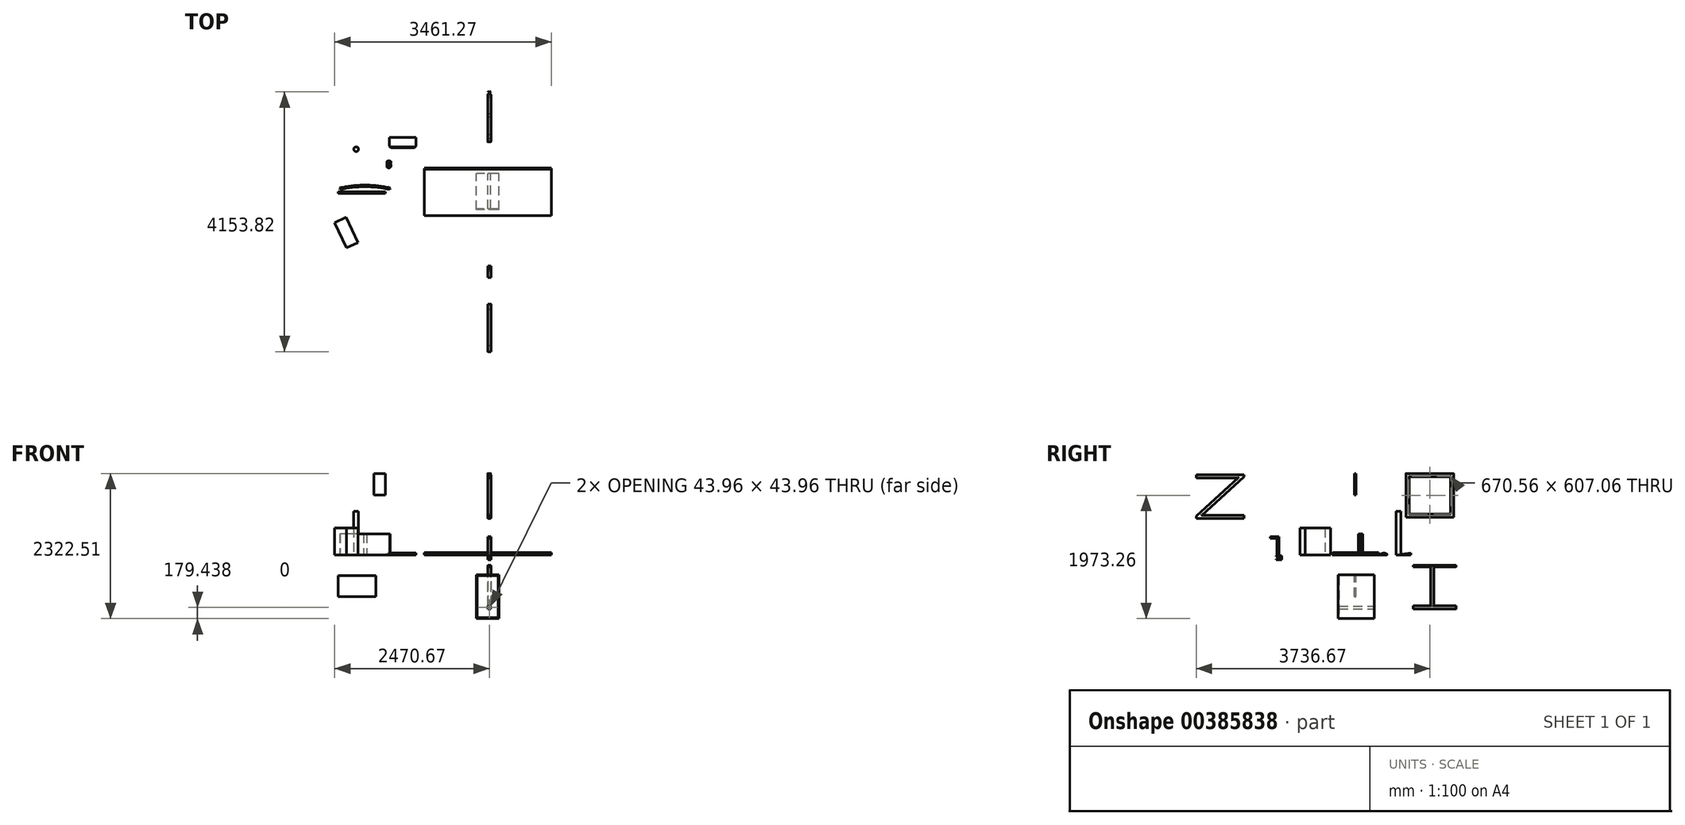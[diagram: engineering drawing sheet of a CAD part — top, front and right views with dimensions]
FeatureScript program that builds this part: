
annotation { "Feature Type Name" : "Feature", "Feature Type Description" : "" }
export const myFeature = defineFeature(function(context is Context, id is Id, definition is map)
    precondition{}
    {
        {
            var Q0;
            Q0=qCreatedBy(makeId("Top.planeOp"),FACE);
            var sketch = newSketch(context, id + "F0", { "sketchPlane" : qUnion([Q0])});
            skLineSegment(sketch, "E0.bottom", {"start": v(1016, -381) * mm, "end": v(-1016, -381) * mm});
            skLineSegment(sketch, "E0.top", {"start": v(1016, 381) * mm, "end": v(-1016, 381) * mm});
            skLineSegment(sketch, "E0.left", {"start": v(1016, -381) * mm, "end": v(1016, 381) * mm});
            skLineSegment(sketch, "E0.right", {"start": v(-1016, -381) * mm, "end": v(-1016, 381) * mm});
            skPoint(sketch, "E0.middle", {"position": v(0, 0) * mm});
            skSolve(sketch);
        }
        {
            var Q0;
            Q0=makeQuery(id+"F0.imprint","IMPRINT",FACE,{"disambiguationData":[TD([[makeQuery(id+"F0.imprint","IMPRINT",EDGE,{"derivedFrom":sQuery(id+"F0.wireOp",EDGE,"E0.bottom")}),-1.0]])]});
            extrude(context, id + "F1", {"entities" : qUnion([Q0]), "depth" : 38.1 * mm});
        }
        {
            var Q0;
            Q0=makeQuery(id+"F1.opExtrude","CAP_EDGE",EDGE,{"disambiguationData":[OSD([sQuery(id+"F0.wireOp",EDGE,"E0.bottom")])],"isStart":false});
            fillet(context, id + "F2", {"entities" : qUnion([Q0]), "radius" : 12.7 * mm, "tangentPropagation" : true, "allowEdgeOverflow" : false});
        }
        {
            var Q0;
            Q0=qCreatedBy(makeId("Top.planeOp"),FACE);
            cPlane(context, id + "F3", {"entities" : qUnion([Q0]), "cplaneType" : CPlaneType.OFFSET, "offset" : 1016 * mm, "oppositeDirection" : true, "width" : 152.4 * mm, "height" : 152.4 * mm});
        }
        {
            var Q0;
            Q0=qCreatedBy(id+"F3.planeOp",FACE);
            var sketch = newSketch(context, id + "F4", { "sketchPlane" : qUnion([Q0])});
            skLineSegment(sketch, "E1.bottom", {"start": v(179.32, -290.83) * mm, "end": v(-179.32, -290.83) * mm});
            skLineSegment(sketch, "E1.top", {"start": v(179.32, 290.83) * mm, "end": v(-179.32, 290.83) * mm});
            skLineSegment(sketch, "E1.left", {"start": v(179.32, -290.83) * mm, "end": v(179.32, 290.83) * mm});
            skLineSegment(sketch, "E1.right", {"start": v(-179.32, -290.83) * mm, "end": v(-179.32, 290.83) * mm});
            skPoint(sketch, "E1.middle", {"position": v(0, 0) * mm});
            skSolve(sketch);
        }
        {
            var Q0;
            Q0 = qSketchRegion(id + "F4", true);
            extrude(context, id + "F5", {"entities" : qUnion([Q0]), "depth" : 698.5 * mm});
        }
        {
            var Q0;
            Q0=makeQuery(id+"F5.opExtrude","SWEPT_FACE",FACE,{"disambiguationData":[OSD([sQuery(id+"F4.wireOp",EDGE,"E1.bottom")])]});
            var sketch = newSketch(context, id + "F6", { "sketchPlane" : qUnion([Q0])});
            skLineSegment(sketch, "E2.0", {"start": v(166.62, -330.2) * mm, "end": v(166.62, -1003.3) * mm});
            skLineSegment(sketch, "E2.1", {"start": v(166.62, -330.2) * mm, "end": v(-166.62, -330.2) * mm});
            skLineSegment(sketch, "E2.2", {"start": v(-166.62, -330.2) * mm, "end": v(-166.62, -1003.3) * mm});
            skLineSegment(sketch, "E2.3", {"start": v(166.62, -1003.3) * mm, "end": v(-166.62, -1003.3) * mm});
            skSolve(sketch);
        }
        {
            var Q0;
            Q0 = qSketchRegion(id + "F6", true);
            extrude(context, id + "F7", {"entities" : qUnion([Q0]), "operationType" : NewBodyOperationType.REMOVE, "oppositeDirection" : true, "depth" : 12.7 * mm});
        }
        {
            var Q0;
            Q0=qCreatedBy(makeId("Right.planeOp"),FACE);
            var sketch = newSketch(context, id + "F8", { "sketchPlane" : qUnion([Q0])});
            skLineSegment(sketch, "E3", {"start": v(1595.15, -163.46) * mm, "end": v(1595.15, -188.86) * mm});
            skLineSegment(sketch, "E4", {"start": v(1595.15, -188.86) * mm, "end": v(1239.55, -188.86) * mm});
            skLineSegment(sketch, "E5", {"start": v(1239.55, -188.86) * mm, "end": v(1239.55, -811.16) * mm});
            skLineSegment(sketch, "E6", {"start": v(1239.55, -811.16) * mm, "end": v(1595.15, -811.16) * mm});
            skLineSegment(sketch, "E7", {"start": v(1595.15, -811.16) * mm, "end": v(1595.15, -861.96) * mm});
            skLineSegment(sketch, "E8", {"start": v(1595.15, -861.96) * mm, "end": v(909.35, -861.96) * mm});
            skLineSegment(sketch, "E9", {"start": v(909.35, -861.96) * mm, "end": v(909.35, -811.16) * mm});
            skLineSegment(sketch, "E10", {"start": v(909.35, -811.16) * mm, "end": v(1188.75, -811.16) * mm});
            skLineSegment(sketch, "E11", {"start": v(1188.75, -811.16) * mm, "end": v(1188.75, -188.86) * mm});
            skLineSegment(sketch, "E12", {"start": v(1188.75, -188.86) * mm, "end": v(909.35, -188.86) * mm});
            skLineSegment(sketch, "E13", {"start": v(909.35, -188.86) * mm, "end": v(909.35, -163.46) * mm});
            skLineSegment(sketch, "E14", {"start": v(1595.15, -163.46) * mm, "end": v(909.35, -163.46) * mm});
            skSolve(sketch);
        }
        {
            var Q0;
            Q0=makeQuery(id+"F8.imprint","IMPRINT",FACE,{"disambiguationData":[TD([[makeQuery(id+"F8.imprint","IMPRINT",EDGE,{"derivedFrom":sQuery(id+"F8.wireOp",EDGE,"E3")}),-1.0]])]});
            extrude(context, id + "F9", {"entities" : qUnion([Q0]), "depth" : 50.8 * mm});
        }
        {
            var Q0;
            Q0=makeQuery(id+"F9.opExtrude","CAP_EDGE",EDGE,{"disambiguationData":[OSD([sQuery(id+"F8.wireOp",EDGE,"E6")])],"isStart":false});
            var Q1;
            Q1=makeQuery(id+"F9.opExtrude","CAP_EDGE",EDGE,{"disambiguationData":[OSD([sQuery(id+"F8.wireOp",EDGE,"E8")])],"isStart":false});
            var Q2;
            Q2=makeQuery(id+"F9.opExtrude","CAP_EDGE",EDGE,{"disambiguationData":[OSD([sQuery(id+"F8.wireOp",EDGE,"E10")])],"isStart":false});
            var Q3;
            Q3=makeQuery(id+"F9.opExtrude","CAP_EDGE",EDGE,{"disambiguationData":[OSD([sQuery(id+"F8.wireOp",EDGE,"E11")])],"isStart":false});
            var Q4;
            Q4=makeQuery(id+"F9.opExtrude","CAP_EDGE",EDGE,{"disambiguationData":[OSD([sQuery(id+"F8.wireOp",EDGE,"E5")])],"isStart":false});
            var Q5;
            Q5=makeQuery(id+"F9.opExtrude","CAP_EDGE",EDGE,{"disambiguationData":[OSD([sQuery(id+"F8.wireOp",EDGE,"E5")])],"isStart":true});
            var Q6;
            Q6=makeQuery(id+"F9.opExtrude","CAP_EDGE",EDGE,{"disambiguationData":[OSD([sQuery(id+"F8.wireOp",EDGE,"E6")])],"isStart":true});
            var Q7;
            Q7=makeQuery(id+"F9.opExtrude","CAP_EDGE",EDGE,{"disambiguationData":[OSD([sQuery(id+"F8.wireOp",EDGE,"E10")])],"isStart":true});
            var Q8;
            Q8=makeQuery(id+"F9.opExtrude","CAP_EDGE",EDGE,{"disambiguationData":[OSD([sQuery(id+"F8.wireOp",EDGE,"E8")])],"isStart":true});
            var Q9;
            Q9=makeQuery(id+"F9.opExtrude","CAP_EDGE",EDGE,{"disambiguationData":[OSD([sQuery(id+"F8.wireOp",EDGE,"E11")])],"isStart":true});
            var Q10;
            Q10=makeQuery(id+"F9.opExtrude","CAP_EDGE",EDGE,{"disambiguationData":[OSD([sQuery(id+"F8.wireOp",EDGE,"E14")])],"isStart":true});
            var Q11;
            Q11=makeQuery(id+"F9.opExtrude","CAP_EDGE",EDGE,{"disambiguationData":[OSD([sQuery(id+"F8.wireOp",EDGE,"E12")])],"isStart":true});
            var Q12;
            Q12=makeQuery(id+"F9.opExtrude","CAP_EDGE",EDGE,{"disambiguationData":[OSD([sQuery(id+"F8.wireOp",EDGE,"E4")])],"isStart":true});
            var Q13;
            Q13=makeQuery(id+"F9.opExtrude","CAP_EDGE",EDGE,{"disambiguationData":[OSD([sQuery(id+"F8.wireOp",EDGE,"E14")])],"isStart":false});
            var Q14;
            Q14=makeQuery(id+"F9.opExtrude","CAP_EDGE",EDGE,{"disambiguationData":[OSD([sQuery(id+"F8.wireOp",EDGE,"E4")])],"isStart":false});
            var Q15;
            Q15=makeQuery(id+"F9.opExtrude","CAP_EDGE",EDGE,{"disambiguationData":[OSD([sQuery(id+"F8.wireOp",EDGE,"E12")])],"isStart":false});
            fillet(context, id + "F10", {"entities" : qUnion([Q0, Q1, Q2, Q3, Q4, Q5, Q6, Q7, Q8, Q9, Q10, Q11, Q12, Q13, Q14, Q15]), "radius" : 5.08 * mm, "tangentPropagation" : true, "allowEdgeOverflow" : false});
        }
        {
            var Q0;
            Q0=makeQuery(id+"F9.opExtrude","SWEPT_FACE",FACE,{"disambiguationData":[OSD([sQuery(id+"F8.wireOp",EDGE,"E7")])]});
            var sketch = newSketch(context, id + "F11", { "sketchPlane" : qUnion([Q0])});
            skLineSegment(sketch, "E15.bottom", {"start": v(-5.96, -858.54) * mm, "end": v(-44.84, -858.54) * mm});
            skLineSegment(sketch, "E15.top", {"start": v(-5.96, -814.58) * mm, "end": v(-44.84, -814.58) * mm});
            skLineSegment(sketch, "E15.left", {"start": v(-3.42, -856) * mm, "end": v(-3.42, -817.12) * mm});
            skLineSegment(sketch, "E15.right", {"start": v(-47.38, -856) * mm, "end": v(-47.38, -817.12) * mm});
            skPoint(sketch, "E15.middle", {"position": v(-25.4, -836.56) * mm});
            skPoint(sketch, "E16.trimOffspring.end.orphan", {"position": v(-1.49, -860.47) * mm});
            skPoint(sketch, "E17.start.orphan", {"position": v(-49.31, -812.65) * mm});
            skPoint(sketch, "E18.visualSharp", {"position": v(-47.38, -814.58) * mm});
            skArc(sketch, "E18.filletArc", {"start": v(-44.84, -814.58) * mm, "mid": v(-46.64, -815.32) * mm, "end": v(-47.38, -817.12) * mm});
            skPoint(sketch, "E19.visualSharp", {"position": v(-47.38, -858.54) * mm});
            skArc(sketch, "E19.filletArc", {"start": v(-47.38, -856) * mm, "mid": v(-46.64, -857.8) * mm, "end": v(-44.84, -858.54) * mm});
            skPoint(sketch, "E20.visualSharp", {"position": v(-3.42, -858.54) * mm});
            skArc(sketch, "E20.filletArc", {"start": v(-5.96, -858.54) * mm, "mid": v(-4.16, -857.8) * mm, "end": v(-3.42, -856) * mm});
            skPoint(sketch, "E21.visualSharp", {"position": v(-3.42, -814.58) * mm});
            skArc(sketch, "E21.filletArc", {"start": v(-3.42, -817.12) * mm, "mid": v(-4.16, -815.32) * mm, "end": v(-5.96, -814.58) * mm});
            skSolve(sketch);
        }
        {
            var Q0;
            Q0 = qSketchRegion(id + "F11", true);
            extrude(context, id + "F12", {"entities" : qUnion([Q0]), "operationType" : NewBodyOperationType.REMOVE, "endBound" : BoundingType.THROUGH_ALL, "oppositeDirection" : true, "depth" : 25.4 * mm});
        }
        {
            var Q0;
            Q0=qCreatedBy(makeId("Top.planeOp"),FACE);
            var sketch = newSketch(context, id + "F13", { "sketchPlane" : qUnion([Q0])});
            skLineSegment(sketch, "E22", {"start": v(-2361.1, 34.13) * mm, "end": v(-1563.54, 34.13) * mm, "construction": true});
            skArc(sketch, "E23", {"start": v(-1563.54, 34.13) * mm, "mid": v(-1962.32, 78.9) * mm, "end": v(-2361.1, 34.13) * mm});
            skArc(sketch, "E24.0.1.0", {"start": v(-1563.54, 59.53) * mm, "mid": v(-1962.32, 104.3) * mm, "end": v(-2361.1, 59.53) * mm});
            skLineSegment(sketch, "E24.direction1", {"start": v(-1962.32, -1719.42) * mm, "end": v(-1848.02, -1719.42) * mm, "construction": true});
            skLineSegment(sketch, "E24.direction2", {"start": v(-1962.32, -1719.42) * mm, "end": v(-1962.32, -1694.02) * mm, "construction": true});
            skLineSegment(sketch, "E25", {"start": v(-2361.1, 34.13) * mm, "end": v(-2373.8, 34.13) * mm});
            skLineSegment(sketch, "E26", {"start": v(-2373.8, 34.13) * mm, "end": v(-2361.1, 59.53) * mm});
            skLineSegment(sketch, "E27", {"start": v(-1563.54, 34.13) * mm, "end": v(-1550.84, 34.13) * mm});
            skLineSegment(sketch, "E28", {"start": v(-1550.84, 34.13) * mm, "end": v(-1563.54, 59.53) * mm});
            skSolve(sketch);
        }
        {
            var Q0;
            Q0 = qSketchRegion(id + "F13", true);
            extrude(context, id + "F14", {"entities" : qUnion([Q0]), "depth" : 340.36 * mm});
        }
        {
            var Q0;
            Q0=qCreatedBy(makeId("Front.planeOp"),FACE);
            var sketch = newSketch(context, id + "F15", { "sketchPlane" : qUnion([Q0])});
            skLineSegment(sketch, "E29.bottom", {"start": v(-1789.8, -664.85) * mm, "end": v(-2389.23, -664.85) * mm});
            skLineSegment(sketch, "E29.top", {"start": v(-1789.8, -324.49) * mm, "end": v(-2389.23, -324.49) * mm});
            skLineSegment(sketch, "E29.left", {"start": v(-1789.8, -664.85) * mm, "end": v(-1789.8, -324.49) * mm});
            skLineSegment(sketch, "E29.right", {"start": v(-2389.23, -664.85) * mm, "end": v(-2389.23, -324.49) * mm});
            skPoint(sketch, "E29.middle", {"position": v(-2089.51, -494.67) * mm});
            skSolve(sketch);
        }
        {
            var Q0;
            Q0 = qSketchRegion(id + "F15", true);
            extrude(context, id + "F16", {"entities" : qUnion([Q0]), "depth" : 25.4 * mm});
        }
        {
            var Q0;
            Q0=qCreatedBy(makeId("Right.planeOp"),FACE);
            var sketch = newSketch(context, id + "F17", { "sketchPlane" : qUnion([Q0])});
            skLineSegment(sketch, "E30", {"start": v(-1280.87, -22.9) * mm, "end": v(-1204.67, -22.9) * mm});
            skLineSegment(sketch, "E31", {"start": v(-1204.67, -22.9) * mm, "end": v(-1204.67, -61) * mm});
            skLineSegment(sketch, "E32", {"start": v(-1204.67, -61) * mm, "end": v(-1280.87, -61) * mm});
            skLineSegment(sketch, "E33", {"start": v(-1280.87, -61) * mm, "end": v(-1280.87, -73.7) * mm});
            skLineSegment(sketch, "E34", {"start": v(-1280.87, -73.7) * mm, "end": v(-1191.97, -73.7) * mm});
            skLineSegment(sketch, "E35", {"start": v(-1191.97, -73.7) * mm, "end": v(-1191.97, -10.2) * mm});
            skLineSegment(sketch, "E36", {"start": v(-1191.97, -10.2) * mm, "end": v(-1235.72, -10.2) * mm});
            skLineSegment(sketch, "E37", {"start": v(-1235.72, -10.2) * mm, "end": v(-1235.72, 294.6) * mm});
            skLineSegment(sketch, "E38", {"start": v(-1235.72, 294.6) * mm, "end": v(-1372.65, 294.6) * mm});
            skLineSegment(sketch, "E39", {"start": v(-1372.65, 294.6) * mm, "end": v(-1372.65, 269.2) * mm});
            skLineSegment(sketch, "E40", {"start": v(-1372.65, 269.2) * mm, "end": v(-1268.74, 269.2) * mm});
            skLineSegment(sketch, "E41", {"start": v(-1268.74, 269.2) * mm, "end": v(-1268.74, -10.2) * mm});
            skLineSegment(sketch, "E42", {"start": v(-1280.87, -10.2) * mm, "end": v(-1280.87, -22.9) * mm});
            skLineSegment(sketch, "E43", {"start": v(-1268.74, -10.2) * mm, "end": v(-1280.87, -10.2) * mm});
            skSolve(sketch);
        }
        {
            var Q0;
            Q0 = qSketchRegion(id + "F17", true);
            extrude(context, id + "F18", {"entities" : qUnion([Q0]), "depth" : 50.8 * mm});
        }
        {
            var Q0;
            Q0=makeQuery(id+"F14.opExtrude","CAP_FACE",FACE,{"disambiguationData":[OSD([sQuery(id+"F13.wireOp",EDGE,"E23"),sQuery(id+"F13.wireOp",EDGE,"E24.0.1.0"),sQuery(id+"F13.wireOp",EDGE,"E25"),sQuery(id+"F13.wireOp",EDGE,"E26"),sQuery(id+"F13.wireOp",EDGE,"E27"),sQuery(id+"F13.wireOp",EDGE,"E28")])],"isStart":false});
            var sketch = newSketch(context, id + "F19", { "sketchPlane" : qUnion([Q0])});
            skLineSegment(sketch, "E44.bottom", {"start": v(-1936.92, 107.7) * mm, "end": v(-1987.72, 107.7) * mm});
            skLineSegment(sketch, "E44.top", {"start": v(-1936.92, 100.9) * mm, "end": v(-1987.72, 100.9) * mm});
            skLineSegment(sketch, "E44.left", {"start": v(-1936.92, 107.7) * mm, "end": v(-1936.92, 100.9) * mm});
            skLineSegment(sketch, "E44.right", {"start": v(-1987.72, 107.7) * mm, "end": v(-1987.72, 100.9) * mm});
            skPoint(sketch, "E44.middle", {"position": v(-1962.32, 104.3) * mm});
            skSolve(sketch);
        }
        {
            var Q0;
            Q0 = qSketchRegion(id + "F19", true);
            extrude(context, id + "F20", {"entities" : qUnion([Q0]), "operationType" : NewBodyOperationType.ADD, "oppositeDirection" : true, "depth" : 340.36 * mm});
        }
        {
            var Q0;
            Q0=makeQuery(id+"F20.boolean.opBoolean","MERGE",FACE,{"derivedFrom":[makeQuery(id+"F14.opExtrude","CAP_FACE",FACE,{"disambiguationData":[OSD([sQuery(id+"F13.wireOp",EDGE,"E23"),sQuery(id+"F13.wireOp",EDGE,"E24.0.1.0"),sQuery(id+"F13.wireOp",EDGE,"E25"),sQuery(id+"F13.wireOp",EDGE,"E26"),sQuery(id+"F13.wireOp",EDGE,"E27"),sQuery(id+"F13.wireOp",EDGE,"E28")])],"isStart":false}),makeQuery(id+"F20.opExtrude","CAP_FACE",FACE,{"disambiguationData":[OSD([sQuery(id+"F19.wireOp",EDGE,"E44.bottom"),sQuery(id+"F19.wireOp",EDGE,"E44.top"),sQuery(id+"F19.wireOp",EDGE,"E44.left"),sQuery(id+"F19.wireOp",EDGE,"E44.right")])],"isStart":true})]});
            var sketch = newSketch(context, id + "F21", { "sketchPlane" : qUnion([Q0])});
            skLineSegment(sketch, "E45", {"start": v(-2361.1, 34.13) * mm, "end": v(-2370.03, 75.5) * mm});
            skLineSegment(sketch, "E46", {"start": v(-2370.03, 75.5) * mm, "end": v(-2381.81, 26.86) * mm});
            skLineSegment(sketch, "E47", {"start": v(-2381.81, 26.86) * mm, "end": v(-2362.2, 27.05) * mm});
            skLineSegment(sketch, "E48", {"start": v(-2362.2, 27.05) * mm, "end": v(-2361.1, 34.13) * mm});
            skSolve(sketch);
        }
        {
            var Q0;
            Q0 = qSketchRegion(id + "F21", true);
            extrude(context, id + "F22", {"entities" : qUnion([Q0]), "operationType" : NewBodyOperationType.REMOVE, "oppositeDirection" : true, "depth" : 635 * mm});
        }
        {
            var Q0;
            Q0=qCreatedBy(makeId("Top.planeOp"),FACE);
            var sketch = newSketch(context, id + "F23", { "sketchPlane" : qUnion([Q0])});
            skLineSegment(sketch, "E49.bottom", {"start": v(-2076.25, -814.48) * mm, "end": v(-2276.14, -814.48) * mm});
            skLineSegment(sketch, "E49.top", {"start": v(-2076.25, -369.98) * mm, "end": v(-2276.14, -369.98) * mm});
            skLineSegment(sketch, "E49.left", {"start": v(-2076.25, -814.48) * mm, "end": v(-2076.25, -369.98) * mm});
            skLineSegment(sketch, "E49.right", {"start": v(-2276.14, -814.48) * mm, "end": v(-2276.14, -369.98) * mm});
            skPoint(sketch, "E49.middle", {"position": v(-2176.2, -592.23) * mm});
            skSolve(sketch);
        }
        {
            var Q0;
            Q0 = qSketchRegion(id + "F23", true);
            extrude(context, id + "F24", {"entities" : qUnion([Q0]), "depth" : 431.8 * mm});
        }
        {
            var Q0;
            Q0=makeQuery(id+"F24.opExtrude","SWEPT_BODY",BODY,{"disambiguationData":[OSD([sQuery(id+"F23.wireOp",EDGE,"E49.bottom"),sQuery(id+"F23.wireOp",EDGE,"E49.top"),sQuery(id+"F23.wireOp",EDGE,"E49.left"),sQuery(id+"F23.wireOp",EDGE,"E49.right")])]});
            var Q1;
            Q1=makeQuery(id+"F24.opExtrude","SWEPT_EDGE",EDGE,{"disambiguationData":[OSD([sQuery(id+"F23.wireOp",EDGE,"E49.bottom"),sQuery(id+"F23.wireOp",EDGE,"E49.left")])]});
            transform(context, id + "F25", {"entities" : qUnion([Q0]), "transformType" : TransformType.ROTATION, "transformAxis" : qUnion([Q1]), "angle" : 335 * degree, "makeCopy" : false});
        }
        {
            var Q0;
            Q0=qCreatedBy(makeId("Right.planeOp"),FACE);
            var sketch = newSketch(context, id + "F26", { "sketchPlane" : qUnion([Q0])});
            skLineSegment(sketch, "E50.bottom", {"start": v(1559, 608) * mm, "end": v(797, 608) * mm});
            skLineSegment(sketch, "E50.top", {"start": v(1559, 1306.5) * mm, "end": v(797, 1306.5) * mm});
            skLineSegment(sketch, "E50.left", {"start": v(1559, 608) * mm, "end": v(1559, 1306.5) * mm});
            skLineSegment(sketch, "E50.right", {"start": v(797, 608) * mm, "end": v(797, 1306.5) * mm});
            skPoint(sketch, "E50.middle", {"position": v(1178, 957.26) * mm});
            skLineSegment(sketch, "E51.0", {"start": v(1508.2, 1255.7) * mm, "end": v(847.8, 1255.7) * mm});
            skLineSegment(sketch, "E51.1", {"start": v(1508.2, 658.8) * mm, "end": v(1508.2, 1255.7) * mm});
            skLineSegment(sketch, "E51.2", {"start": v(1508.2, 658.8) * mm, "end": v(847.8, 658.8) * mm});
            skLineSegment(sketch, "E51.3", {"start": v(847.8, 658.8) * mm, "end": v(847.8, 1255.7) * mm});
            skSolve(sketch);
        }
        {
            var Q0;
            Q0=makeQuery(id+"F26.imprint","IMPRINT",FACE,{"disambiguationData":[TD([[makeQuery(id+"F26.imprint","IMPRINT",EDGE,{"derivedFrom":sQuery(id+"F26.wireOp",EDGE,"E50.bottom")}),-1.0]])]});
            extrude(context, id + "F27", {"entities" : qUnion([Q0]), "depth" : 50.8 * mm});
        }
        {
            var Q0;
            Q0=qCreatedBy(makeId("Top.planeOp"),FACE);
            var sketch = newSketch(context, id + "F28", { "sketchPlane" : qUnion([Q0])});
            skCircle(sketch, "E52", {"center": v(-2102.7, 679.67) * mm, "radius": 38.1 * mm});
            skSolve(sketch);
        }
        {
            var Q0;
            Q0 = qSketchRegion(id + "F28", true);
            extrude(context, id + "F29", {"entities" : qUnion([Q0]), "depth" : 698.5 * mm});
        }
        {
            var Q0;
            Q0=makeQuery(id+"F27.opExtrude","CAP_EDGE",EDGE,{"disambiguationData":[OSD([sQuery(id+"F26.wireOp",EDGE,"E50.right")])],"isStart":false});
            var Q1;
            Q1=makeQuery(id+"F27.opExtrude","CAP_EDGE",EDGE,{"disambiguationData":[OSD([sQuery(id+"F26.wireOp",EDGE,"E50.right")])],"isStart":true});
            var Q2;
            Q2=makeQuery(id+"F27.opExtrude","CAP_EDGE",EDGE,{"disambiguationData":[OSD([sQuery(id+"F26.wireOp",EDGE,"E51.3")])],"isStart":false});
            var Q3;
            Q3=makeQuery(id+"F27.opExtrude","CAP_EDGE",EDGE,{"disambiguationData":[OSD([sQuery(id+"F26.wireOp",EDGE,"E51.2")])],"isStart":false});
            var Q4;
            Q4=makeQuery(id+"F27.opExtrude","CAP_EDGE",EDGE,{"disambiguationData":[OSD([sQuery(id+"F26.wireOp",EDGE,"E50.bottom")])],"isStart":false});
            var Q5;
            Q5=makeQuery(id+"F27.opExtrude","CAP_EDGE",EDGE,{"disambiguationData":[OSD([sQuery(id+"F26.wireOp",EDGE,"E51.2")])],"isStart":true});
            var Q6;
            Q6=makeQuery(id+"F27.opExtrude","CAP_EDGE",EDGE,{"disambiguationData":[OSD([sQuery(id+"F26.wireOp",EDGE,"E50.bottom")])],"isStart":true});
            var Q7;
            Q7=makeQuery(id+"F27.opExtrude","CAP_EDGE",EDGE,{"disambiguationData":[OSD([sQuery(id+"F26.wireOp",EDGE,"E51.3")])],"isStart":true});
            var Q8;
            Q8=makeQuery(id+"F27.opExtrude","CAP_EDGE",EDGE,{"disambiguationData":[OSD([sQuery(id+"F26.wireOp",EDGE,"E51.1")])],"isStart":true});
            var Q9;
            Q9=makeQuery(id+"F27.opExtrude","CAP_EDGE",EDGE,{"disambiguationData":[OSD([sQuery(id+"F26.wireOp",EDGE,"E51.1")])],"isStart":false});
            var Q10;
            Q10=makeQuery(id+"F27.opExtrude","CAP_EDGE",EDGE,{"disambiguationData":[OSD([sQuery(id+"F26.wireOp",EDGE,"E50.left")])],"isStart":true});
            var Q11;
            Q11=makeQuery(id+"F27.opExtrude","CAP_EDGE",EDGE,{"disambiguationData":[OSD([sQuery(id+"F26.wireOp",EDGE,"E50.left")])],"isStart":false});
            var Q12;
            Q12=makeQuery(id+"F27.opExtrude","CAP_EDGE",EDGE,{"disambiguationData":[OSD([sQuery(id+"F26.wireOp",EDGE,"E50.top")])],"isStart":false});
            var Q13;
            Q13=makeQuery(id+"F27.opExtrude","CAP_EDGE",EDGE,{"disambiguationData":[OSD([sQuery(id+"F26.wireOp",EDGE,"E51.0")])],"isStart":false});
            var Q14;
            Q14=makeQuery(id+"F27.opExtrude","CAP_EDGE",EDGE,{"disambiguationData":[OSD([sQuery(id+"F26.wireOp",EDGE,"E50.top")])],"isStart":true});
            var Q15;
            Q15=makeQuery(id+"F27.opExtrude","CAP_EDGE",EDGE,{"disambiguationData":[OSD([sQuery(id+"F26.wireOp",EDGE,"E51.0")])],"isStart":true});
            fillet(context, id + "F30", {"entities" : qUnion([Q0, Q1, Q2, Q3, Q4, Q5, Q6, Q7, Q8, Q9, Q10, Q11, Q12, Q13, Q14, Q15]), "radius" : 5.08 * mm, "tangentPropagation" : true, "allowEdgeOverflow" : false});
        }
        {
            var Q0;
            Q0=qCreatedBy(makeId("Right.planeOp"),FACE);
            var sketch = newSketch(context, id + "F31", { "sketchPlane" : qUnion([Q0])});
            skLineSegment(sketch, "E53.bottom", {"start": v(-1796.67, 587.81) * mm, "end": v(-2558.67, 587.81) * mm});
            skLineSegment(sketch, "E53.top", {"start": v(-1796.67, 1286.31) * mm, "end": v(-2558.67, 1286.31) * mm});
            skLineSegment(sketch, "E53.left", {"start": v(-1796.67, 587.81) * mm, "end": v(-1796.67, 638.61) * mm});
            skLineSegment(sketch, "E53.right", {"start": v(-2558.67, 587.81) * mm, "end": v(-2558.67, 622.27) * mm});
            skPoint(sketch, "E53.middle", {"position": v(-2177.67, 937.06) * mm});
            skLineSegment(sketch, "E54.0", {"start": v(-1796.67, 638.61) * mm, "end": v(-2465.66, 638.61) * mm});
            skLineSegment(sketch, "E55.0", {"start": v(-1889.68, 1235.51) * mm, "end": v(-2558.67, 622.27) * mm});
            skLineSegment(sketch, "E56.0", {"start": v(-1796.67, 1251.86) * mm, "end": v(-2465.66, 638.61) * mm});
            skLineSegment(sketch, "E57.trimOffspring", {"start": v(-2558.67, 1235.51) * mm, "end": v(-2558.67, 1286.31) * mm});
            skLineSegment(sketch, "E58.trimOffspring", {"start": v(-1889.68, 1235.51) * mm, "end": v(-2558.67, 1235.51) * mm});
            skLineSegment(sketch, "E59.trimOffspring", {"start": v(-1796.67, 1251.86) * mm, "end": v(-1796.67, 1286.31) * mm});
            skSolve(sketch);
        }
        {
            var Q0;
            Q0 = qSketchRegion(id + "F31", true);
            extrude(context, id + "F32", {"entities" : qUnion([Q0]), "depth" : 50.8 * mm});
        }
        {
            var Q0;
            Q0=makeQuery(id+"F32.opExtrude","CAP_EDGE",EDGE,{"disambiguationData":[OSD([sQuery(id+"F31.wireOp",EDGE,"E53.top")])],"isStart":false});
            var Q1;
            Q1=makeQuery(id+"F32.opExtrude","CAP_EDGE",EDGE,{"disambiguationData":[OSD([sQuery(id+"F31.wireOp",EDGE,"E58.trimOffspring")])],"isStart":false});
            var Q2;
            Q2=makeQuery(id+"F32.opExtrude","CAP_EDGE",EDGE,{"disambiguationData":[OSD([sQuery(id+"F31.wireOp",EDGE,"E55.0")])],"isStart":false});
            var Q3;
            Q3=makeQuery(id+"F32.opExtrude","CAP_EDGE",EDGE,{"disambiguationData":[OSD([sQuery(id+"F31.wireOp",EDGE,"E56.0")])],"isStart":false});
            var Q4;
            Q4=makeQuery(id+"F32.opExtrude","CAP_EDGE",EDGE,{"disambiguationData":[OSD([sQuery(id+"F31.wireOp",EDGE,"E53.bottom")])],"isStart":false});
            var Q5;
            Q5=makeQuery(id+"F32.opExtrude","CAP_EDGE",EDGE,{"disambiguationData":[OSD([sQuery(id+"F31.wireOp",EDGE,"E54.0")])],"isStart":false});
            var Q6;
            Q6=makeQuery(id+"F32.opExtrude","CAP_EDGE",EDGE,{"disambiguationData":[OSD([sQuery(id+"F31.wireOp",EDGE,"E53.top")])],"isStart":true});
            var Q7;
            Q7=makeQuery(id+"F32.opExtrude","CAP_EDGE",EDGE,{"disambiguationData":[OSD([sQuery(id+"F31.wireOp",EDGE,"E58.trimOffspring")])],"isStart":true});
            var Q8;
            Q8=makeQuery(id+"F32.opExtrude","CAP_EDGE",EDGE,{"disambiguationData":[OSD([sQuery(id+"F31.wireOp",EDGE,"E55.0")])],"isStart":true});
            var Q9;
            Q9=makeQuery(id+"F32.opExtrude","CAP_EDGE",EDGE,{"disambiguationData":[OSD([sQuery(id+"F31.wireOp",EDGE,"E56.0")])],"isStart":true});
            var Q10;
            Q10=makeQuery(id+"F32.opExtrude","CAP_EDGE",EDGE,{"disambiguationData":[OSD([sQuery(id+"F31.wireOp",EDGE,"E54.0")])],"isStart":true});
            var Q11;
            Q11=makeQuery(id+"F32.opExtrude","CAP_EDGE",EDGE,{"disambiguationData":[OSD([sQuery(id+"F31.wireOp",EDGE,"E53.bottom")])],"isStart":true});
            fillet(context, id + "F33", {"entities" : qUnion([Q0, Q1, Q2, Q3, Q4, Q5, Q6, Q7, Q8, Q9, Q10, Q11]), "radius" : 5.08 * mm, "tangentPropagation" : true, "allowEdgeOverflow" : false});
        }
        {
            var Q0;
            Q0=qCreatedBy(makeId("Front.planeOp"),FACE);
            var sketch = newSketch(context, id + "F34", { "sketchPlane" : qUnion([Q0])});
            skLineSegment(sketch, "E60.bottom", {"start": v(-1631.99, 964.4) * mm, "end": v(-1822.49, 964.4) * mm});
            skLineSegment(sketch, "E60.top", {"start": v(-1631.99, 1304.77) * mm, "end": v(-1822.49, 1304.77) * mm});
            skLineSegment(sketch, "E60.left", {"start": v(-1631.99, 964.4) * mm, "end": v(-1631.99, 1304.77) * mm});
            skLineSegment(sketch, "E60.right", {"start": v(-1822.49, 964.4) * mm, "end": v(-1822.49, 1304.77) * mm});
            skPoint(sketch, "E60.middle", {"position": v(-1727.24, 1134.59) * mm});
            skSolve(sketch);
        }
        {
            var Q0;
            Q0=makeQuery(id+"F34.imprint","IMPRINT",FACE,{"disambiguationData":[TD([[makeQuery(id+"F34.imprint","IMPRINT",EDGE,{"derivedFrom":sQuery(id+"F34.wireOp",EDGE,"E60.bottom")}),-1.0]])]});
            extrude(context, id + "F35", {"entities" : qUnion([Q0]), "depth" : 25.4 * mm});
        }
        {
            var Q0;
            Q0=makeQuery(id+"F20.boolean.opBoolean","MERGE",FACE,{"derivedFrom":[makeQuery(id+"F14.opExtrude","CAP_FACE",FACE,{"disambiguationData":[OSD([sQuery(id+"F13.wireOp",EDGE,"E23"),sQuery(id+"F13.wireOp",EDGE,"E24.0.1.0"),sQuery(id+"F13.wireOp",EDGE,"E25"),sQuery(id+"F13.wireOp",EDGE,"E26"),sQuery(id+"F13.wireOp",EDGE,"E27"),sQuery(id+"F13.wireOp",EDGE,"E28")])],"isStart":false}),makeQuery(id+"F20.opExtrude","CAP_FACE",FACE,{"disambiguationData":[OSD([sQuery(id+"F19.wireOp",EDGE,"E44.bottom"),sQuery(id+"F19.wireOp",EDGE,"E44.top"),sQuery(id+"F19.wireOp",EDGE,"E44.left"),sQuery(id+"F19.wireOp",EDGE,"E44.right")])],"isStart":true})]});
            var sketch = newSketch(context, id + "F36", { "sketchPlane" : qUnion([Q0])});
            skLineSegment(sketch, "E61", {"start": v(-1563.54, 34.13) * mm, "end": v(-1548.2, 105.2) * mm});
            skLineSegment(sketch, "E62", {"start": v(-1548.2, 105.2) * mm, "end": v(-1516.45, 15.34) * mm});
            skLineSegment(sketch, "E63", {"start": v(-1516.45, 15.34) * mm, "end": v(-1570.96, 22.44) * mm});
            skLineSegment(sketch, "E64", {"start": v(-1570.96, 22.44) * mm, "end": v(-1563.54, 34.13) * mm});
            skSolve(sketch);
        }
        {
            var Q0;
            Q0 = qSketchRegion(id + "F36", true);
            extrude(context, id + "F37", {"entities" : qUnion([Q0]), "operationType" : NewBodyOperationType.REMOVE, "endBound" : BoundingType.THROUGH_ALL, "oppositeDirection" : true, "depth" : 25.4 * mm});
        }
        {
            var Q0;
            Q0=qCreatedBy(makeId("Top.planeOp"),FACE);
            var sketch = newSketch(context, id + "F38", { "sketchPlane" : qUnion([Q0])});
            skLineSegment(sketch, "E65.bottom", {"start": v(-1147.1, 705.28) * mm, "end": v(-1569.53, 705.28) * mm});
            skLineSegment(sketch, "E65.top", {"start": v(-1147.1, 870.38) * mm, "end": v(-1569.53, 870.38) * mm});
            skLineSegment(sketch, "E65.left", {"start": v(-1147.1, 705.28) * mm, "end": v(-1147.1, 870.38) * mm});
            skLineSegment(sketch, "E65.right", {"start": v(-1569.53, 705.28) * mm, "end": v(-1569.53, 870.38) * mm});
            skPoint(sketch, "E65.middle", {"position": v(-1358.32, 787.83) * mm});
            skSolve(sketch);
        }
        {
            var Q0;
            Q0 = qSketchRegion(id + "F38", true);
            extrude(context, id + "F39", {"entities" : qUnion([Q0]), "depth" : 50.8 * mm});
        }
        {
            var Q0;
            Q0=makeQuery(id+"F39.opExtrude","SWEPT_FACE",FACE,{"disambiguationData":[OSD([sQuery(id+"F38.wireOp",EDGE,"E65.right")])]});
            var sketch = newSketch(context, id + "F40", { "sketchPlane" : qUnion([Q0])});
            skLineSegment(sketch, "E66", {"start": v(-870.38, 35.68) * mm, "end": v(-717.64, 13.4) * mm});
            skLineSegment(sketch, "E67", {"start": v(-717.64, 13.4) * mm, "end": v(-705.28, 0) * mm});
            skLineSegment(sketch, "E68", {"start": v(-705.28, 0) * mm, "end": v(-705.28, 50.8) * mm});
            skLineSegment(sketch, "E69", {"start": v(-705.28, 50.8) * mm, "end": v(-870.38, 50.8) * mm});
            skLineSegment(sketch, "E70", {"start": v(-870.38, 50.8) * mm, "end": v(-870.38, 35.68) * mm});
            skSolve(sketch);
        }
        {
            var Q0;
            Q0=makeQuery(id+"F40.imprint","IMPRINT",FACE,{"disambiguationData":[TD([[makeQuery(id+"F40.imprint","IMPRINT",EDGE,{"derivedFrom":sQuery(id+"F40.wireOp",EDGE,"E66")}),1.0]])]});
            extrude(context, id + "F41", {"entities" : qUnion([Q0]), "operationType" : NewBodyOperationType.REMOVE, "endBound" : BoundingType.THROUGH_ALL, "oppositeDirection" : true, "depth" : 25.4 * mm});
        }
        {
            var Q0;
            Q0=makeQuery(id+"F39.opExtrude","CAP_FACE",FACE,{"disambiguationData":[OSD([sQuery(id+"F38.wireOp",EDGE,"E65.bottom"),sQuery(id+"F38.wireOp",EDGE,"E65.top"),sQuery(id+"F38.wireOp",EDGE,"E65.left"),sQuery(id+"F38.wireOp",EDGE,"E65.right")])],"isStart":true});
            var sketch = newSketch(context, id + "F42", { "sketchPlane" : qUnion([Q0])});
            skLineSegment(sketch, "E71", {"start": v(-1147.1, -730.68) * mm, "end": v(-1172.5, -705.28) * mm});
            skLineSegment(sketch, "E72", {"start": v(-1172.5, -705.28) * mm, "end": v(-1147.1, -705.28) * mm});
            skLineSegment(sketch, "E73", {"start": v(-1147.1, -705.28) * mm, "end": v(-1147.1, -730.68) * mm});
            skLineSegment(sketch, "E74", {"start": v(-1569.53, -730.68) * mm, "end": v(-1569.53, -705.28) * mm});
            skLineSegment(sketch, "E75", {"start": v(-1569.53, -705.28) * mm, "end": v(-1544.13, -705.28) * mm});
            skLineSegment(sketch, "E76", {"start": v(-1544.13, -705.28) * mm, "end": v(-1569.53, -730.68) * mm});
            skSolve(sketch);
        }
        {
            var Q0;
            Q0 = qSketchRegion(id + "F42", true);
            extrude(context, id + "F43", {"entities" : qUnion([Q0]), "operationType" : NewBodyOperationType.REMOVE, "oppositeDirection" : true, "depth" : 25.4 * mm});
        }
        {
            var Q0;
            Q0=qCreatedBy(makeId("Top.planeOp"),FACE);
            var sketch = newSketch(context, id + "F44", { "sketchPlane" : qUnion([Q0])});
            skLineSegment(sketch, "E77.bottom", {"start": v(-1580.4, 379.1) * mm, "end": v(-1580.4, 379.1) * mm});
            skLineSegment(sketch, "E77.left", {"start": v(-1547.38, 412.12) * mm, "end": v(-1547.38, 482.52) * mm});
            skLineSegment(sketch, "E77.right", {"start": v(-1613.42, 412.12) * mm, "end": v(-1613.42, 483.15) * mm});
            skPoint(sketch, "E77.middle", {"position": v(-1580.4, 436.25) * mm});
            skPoint(sketch, "E78.visualSharp", {"position": v(-1613.42, 379.1) * mm});
            skArc(sketch, "E78.filletArc", {"start": v(-1613.42, 412.12) * mm, "mid": v(-1603.75, 388.77) * mm, "end": v(-1580.4, 379.1) * mm});
            skPoint(sketch, "E79.visualSharp", {"position": v(-1547.38, 379.1) * mm});
            skArc(sketch, "E79.filletArc", {"start": v(-1580.4, 379.1) * mm, "mid": v(-1557.05, 388.77) * mm, "end": v(-1547.38, 412.12) * mm});
            skArc(sketch, "E80", {"start": v(-1547.38, 482.52) * mm, "mid": v(-1580.32, 491.13) * mm, "end": v(-1613.42, 483.15) * mm});
            skPoint(sketch, "E81.orphan", {"position": v(-1547.38, 493.4) * mm});
            skPoint(sketch, "E82.orphan", {"position": v(-1613.42, 493.4) * mm});
            skSolve(sketch);
        }
        {
            var Q0;
            Q0 = qSketchRegion(id + "F44", true);
            extrude(context, id + "F45", {"entities" : qUnion([Q0]), "depth" : 44.45 * mm});
        }
        {
            var Q0;
            Q0=makeQuery(id+"F45.opExtrude","SWEPT_FACE",FACE,{"disambiguationData":[OSD([sQuery(id+"F44.wireOp",EDGE,"E77.right")])]});
            var sketch = newSketch(context, id + "F46", { "sketchPlane" : qUnion([Q0])});
            skArc(sketch, "E83", {"start": v(-375.44, -2.26) * mm, "mid": v(-432.37, 31.57) * mm, "end": v(-495.88, 12.8) * mm});
            skLineSegment(sketch, "E84", {"start": v(-495.88, 12.8) * mm, "end": v(-493.82, 72.13) * mm});
            skLineSegment(sketch, "E85", {"start": v(-493.82, 72.13) * mm, "end": v(-349.76, 62.09) * mm});
            skLineSegment(sketch, "E86", {"start": v(-349.76, 62.09) * mm, "end": v(-375.44, -2.26) * mm});
            skSolve(sketch);
        }
        {
            var Q0;
            Q0 = qSketchRegion(id + "F46", true);
            extrude(context, id + "F47", {"entities" : qUnion([Q0]), "operationType" : NewBodyOperationType.REMOVE, "endBound" : BoundingType.THROUGH_ALL, "oppositeDirection" : true, "depth" : 25.4 * mm});
        }
        {
            var Q0;
            Q0=makeQuery(id+"F45.opExtrude","CAP_FACE",FACE,{"disambiguationData":[OSD([sQuery(id+"F44.wireOp",EDGE,"E77.left"),sQuery(id+"F44.wireOp",EDGE,"E77.right"),sQuery(id+"F44.wireOp",EDGE,"E78.filletArc"),sQuery(id+"F44.wireOp",EDGE,"E79.filletArc"),sQuery(id+"F44.wireOp",EDGE,"E80")])],"isStart":true});
            var sketch = newSketch(context, id + "F48", { "sketchPlane" : qUnion([Q0])});
            skArc(sketch, "E87", {"start": v(-1613.42, -483.15) * mm, "mid": v(-1609.46, -447.64) * mm, "end": v(-1613.42, -412.12) * mm});
            skArc(sketch, "E88", {"start": v(-1547.38, -421.92) * mm, "mid": v(-1550.05, -452.22) * mm, "end": v(-1547.38, -482.52) * mm});
            skLineSegment(sketch, "E89", {"start": v(-1613.42, -412.12) * mm, "end": v(-1631.5, -461.5) * mm});
            skLineSegment(sketch, "E90", {"start": v(-1631.5, -461.5) * mm, "end": v(-1613.42, -483.15) * mm});
            skLineSegment(sketch, "E91", {"start": v(-1547.38, -482.52) * mm, "end": v(-1543.4, -420.43) * mm});
            skLineSegment(sketch, "E92", {"start": v(-1543.4, -420.43) * mm, "end": v(-1547.38, -421.92) * mm});
            skSolve(sketch);
        }
        {
            var Q0;
            Q0 = qSketchRegion(id + "F48", true);
            extrude(context, id + "F49", {"entities" : qUnion([Q0]), "operationType" : NewBodyOperationType.REMOVE, "endBound" : BoundingType.THROUGH_ALL, "oppositeDirection" : true, "depth" : 25.4 * mm});
        }
        {
            var Q0;
            Q0=makeQuery(id+"F49.boolean.opBoolean","INTERSECT",EDGE,{"derivedFrom":[makeQuery(id+"F47.boolean.opBoolean","COPY",FACE,{"derivedFrom":makeQuery(id+"F47.opExtrude","SWEPT_FACE",FACE,{"disambiguationData":[OSD([sQuery(id+"F46.wireOp",EDGE,"E83")])]})}),makeQuery(id+"F49.opExtrude","SWEPT_FACE",FACE,{"disambiguationData":[OSD([sQuery(id+"F48.wireOp",EDGE,"E87")])]})]});
            var Q1;
            Q1=makeQuery(id+"F47.boolean.opBoolean","INTERSECT",EDGE,{"derivedFrom":[makeQuery(id+"F45.opExtrude","SWEPT_FACE",FACE,{"disambiguationData":[OSD([sQuery(id+"F44.wireOp",EDGE,"E78.filletArc"),sQuery(id+"F44.wireOp",EDGE,"E79.filletArc")])]}),makeQuery(id+"F47.opExtrude","SWEPT_FACE",FACE,{"disambiguationData":[OSD([sQuery(id+"F46.wireOp",EDGE,"E83")])]})]});
            var Q2;
            Q2=makeQuery(id+"F49.boolean.opBoolean","INTERSECT",EDGE,{"derivedFrom":[makeQuery(id+"F47.boolean.opBoolean","COPY",FACE,{"derivedFrom":makeQuery(id+"F47.opExtrude","SWEPT_FACE",FACE,{"disambiguationData":[OSD([sQuery(id+"F46.wireOp",EDGE,"E83")])]})}),makeQuery(id+"F49.opExtrude","SWEPT_FACE",FACE,{"disambiguationData":[OSD([sQuery(id+"F48.wireOp",EDGE,"E88")])]})]});
            var Q3;
            Q3=makeQuery(id+"F47.boolean.opBoolean","INTERSECT",EDGE,{"derivedFrom":[makeQuery(id+"F45.opExtrude","SWEPT_FACE",FACE,{"disambiguationData":[OSD([sQuery(id+"F44.wireOp",EDGE,"E77.left")])]}),makeQuery(id+"F47.opExtrude","SWEPT_FACE",FACE,{"disambiguationData":[OSD([sQuery(id+"F46.wireOp",EDGE,"E83")])]})]});
            fillet(context, id + "F50", {"entities" : qUnion([Q0, Q1, Q2, Q3]), "radius" : 20.32 * mm, "tangentPropagation" : true, "allowEdgeOverflow" : false});
        }
    });
